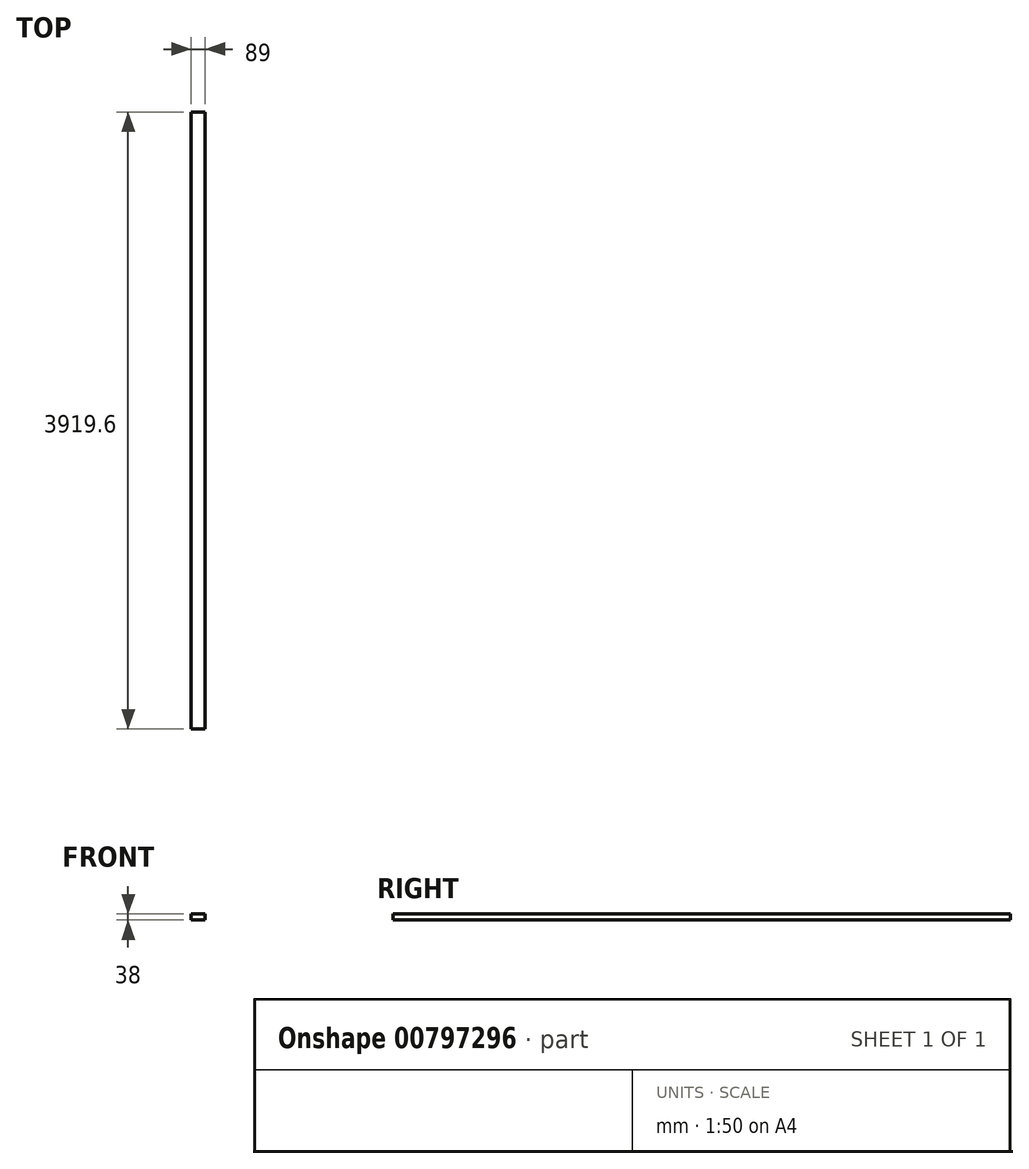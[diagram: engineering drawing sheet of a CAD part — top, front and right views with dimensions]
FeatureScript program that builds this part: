
annotation { "Feature Type Name" : "Feature", "Feature Type Description" : "" }
export const myFeature = defineFeature(function(context is Context, id is Id, definition is map)
    precondition{}
    {
        {
            var Q0;
            Q0=qCreatedBy(makeId("Front.planeOp"),FACE);
            var sketch = newSketch(context, id + "F0", { "sketchPlane" : qUnion([Q0])});
            skLineSegment(sketch, "E0.bottom", {"start": v(44.5, 19) * mm, "end": v(-44.5, 19) * mm});
            skLineSegment(sketch, "E0.top", {"start": v(44.5, -19) * mm, "end": v(-44.5, -19) * mm});
            skLineSegment(sketch, "E0.left", {"start": v(44.5, 19) * mm, "end": v(44.5, -19) * mm});
            skLineSegment(sketch, "E0.right", {"start": v(-44.5, 19) * mm, "end": v(-44.5, -19) * mm});
            skPoint(sketch, "E0.middle", {"position": v(0, 0) * mm});
            skSolve(sketch);
        }
        {
            var Q0;
            Q0 = qSketchRegion(id + "F0", true);
            extrude(context, id + "F1", {"entities" : qUnion([Q0]), "depth" : 3919.6 * mm, "offsetDistance" : 25 * mm, "symmetric" : true});
        }
    });
